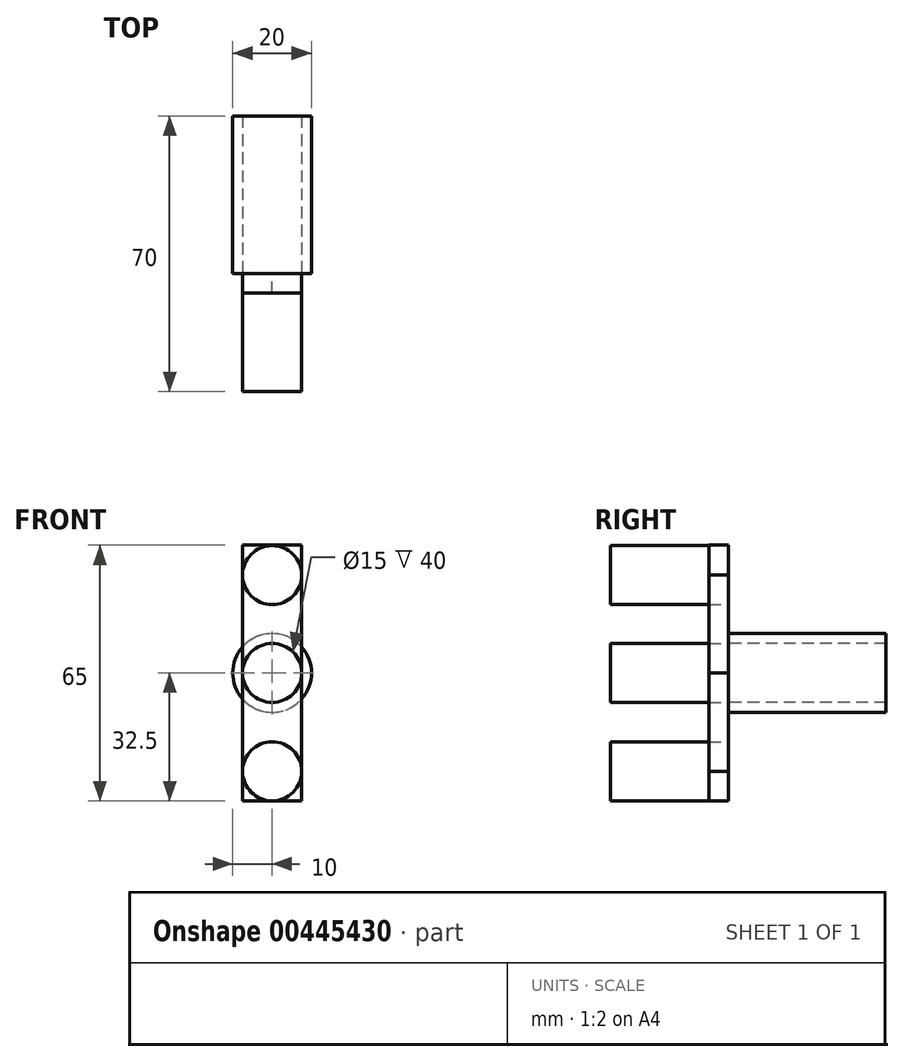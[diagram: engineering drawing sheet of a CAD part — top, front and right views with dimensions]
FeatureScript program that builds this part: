
annotation { "Feature Type Name" : "Feature", "Feature Type Description" : "" }
export const myFeature = defineFeature(function(context is Context, id is Id, definition is map)
    precondition{}
    {
        {
            var Q0;
            Q0=qCreatedBy(makeId("Front.planeOp"),FACE);
            var sketch = newSketch(context, id + "F0", { "sketchPlane" : qUnion([Q0])});
            skLineSegment(sketch, "E0.bottom", {"start": v(-7.5, 32.5) * mm, "end": v(7.5, 32.5) * mm});
            skLineSegment(sketch, "E0.top", {"start": v(-7.5, -32.5) * mm, "end": v(7.5, -32.5) * mm});
            skLineSegment(sketch, "E0.left", {"start": v(-7.5, 32.5) * mm, "end": v(-7.5, -32.5) * mm});
            skLineSegment(sketch, "E0.right", {"start": v(7.5, 32.5) * mm, "end": v(7.5, -32.5) * mm});
            skPoint(sketch, "E0.middle", {"position": v(0, 0) * mm});
            skCircle(sketch, "E1", {"center": v(0, 0) * mm, "radius": 7.5 * mm});
            skLineSegment(sketch, "E2", {"start": v(0, 7.5) * mm, "end": v(0, 17.5) * mm});
            skLineSegment(sketch, "E3", {"start": v(0, -7.5) * mm, "end": v(0, -17.5) * mm});
            skCircle(sketch, "E4", {"center": v(0, -25) * mm, "radius": 7.5 * mm});
            skCircle(sketch, "E5", {"center": v(0, 24.86) * mm, "radius": 7.5 * mm});
            skSolve(sketch);
        }
        {
            var Q0;
            {var subQ0=sQuery(id+"F0.wireOp",EDGE,"E1");var subQ1=makeQuery(id+"F0.imprint","INTERSECT",VERTEX,{"derivedFrom":[subQ0,sQuery(id+"F0.wireOp",EDGE,"E2")]});Q0=makeQuery(id+"F0.imprint","IMPRINT",FACE,{"disambiguationData":[TD([[makeQuery(id+"F0.imprint","IMPRINT",EDGE,{"disambiguationData":[TD([[subQ1,1.0]])],"derivedFrom":subQ0}),1.0]])]});}
            var Q1;
            {var subQ0=sQuery(id+"F0.wireOp",EDGE,"E5");var subQ1=makeQuery(id+"F0.imprint","INTERSECT",VERTEX,{"derivedFrom":[sQuery(id+"F0.wireOp",EDGE,"E0.left"),subQ0]});Q1=makeQuery(id+"F0.imprint","IMPRINT",FACE,{"disambiguationData":[TD([[makeQuery(id+"F0.imprint","IMPRINT",EDGE,{"disambiguationData":[TD([[subQ1,1.0]])],"derivedFrom":subQ0}),1.0]])]});}
            var Q2;
            {var subQ0=sQuery(id+"F0.wireOp",EDGE,"E4");var subQ1=makeQuery(id+"F0.imprint","INTERSECT",VERTEX,{"derivedFrom":[sQuery(id+"F0.wireOp",EDGE,"E3"),subQ0]});Q2=makeQuery(id+"F0.imprint","IMPRINT",FACE,{"disambiguationData":[TD([[makeQuery(id+"F0.imprint","IMPRINT",EDGE,{"disambiguationData":[TD([[subQ1,1.0]])],"derivedFrom":subQ0}),1.0]])]});}
            extrude(context, id + "F1", {"entities" : qUnion([Q0, Q1, Q2]), "depth" : 30 * mm});
        }
        {
            var Q0;
            {var subQ0=sQuery(id+"F0.wireOp",EDGE,"E5");var subQ1=sQuery(id+"F0.wireOp",EDGE,"E0.right");var subQ2=makeQuery(id+"F0.imprint","INTERSECT",VERTEX,{"derivedFrom":[subQ1,subQ0]});Q0=makeQuery(id+"F0.imprint","IMPRINT",FACE,{"disambiguationData":[TD([[makeQuery(id+"F0.imprint","IMPRINT",EDGE,{"disambiguationData":[TD([[subQ2,-1.0]])],"derivedFrom":subQ1}),-1.0]])]});}
            var Q1;
            {var subQ0=sQuery(id+"F0.wireOp",EDGE,"E5");var subQ1=sQuery(id+"F0.wireOp",EDGE,"E0.left");var subQ2=makeQuery(id+"F0.imprint","INTERSECT",VERTEX,{"derivedFrom":[subQ1,subQ0]});Q1=makeQuery(id+"F0.imprint","IMPRINT",FACE,{"disambiguationData":[TD([[makeQuery(id+"F0.imprint","IMPRINT",EDGE,{"disambiguationData":[TD([[subQ2,-1.0]])],"derivedFrom":subQ1}),1.0]])]});}
            var Q2;
            {var subQ0=sQuery(id+"F0.wireOp",EDGE,"E0.bottom");Q2=makeQuery(id+"F0.imprint","IMPRINT",FACE,{"disambiguationData":[TD([[makeQuery(id+"F0.imprint","IMPRINT",EDGE,{"derivedFrom":subQ0}),-1.0]])]});}
            var Q3;
            {var subQ5=sQuery(id+"F0.wireOp",EDGE,"E3");Q3=makeQuery(id+"F0.imprint","IMPRINT",FACE,{"disambiguationData":[TD([[makeQuery(id+"F0.imprint","IMPRINT",EDGE,{"derivedFrom":subQ5}),1.0]])]});}
            var Q4;
            {var subQ5=sQuery(id+"F0.wireOp",EDGE,"E3");Q4=makeQuery(id+"F0.imprint","IMPRINT",FACE,{"disambiguationData":[TD([[makeQuery(id+"F0.imprint","IMPRINT",EDGE,{"derivedFrom":subQ5}),-1.0]])]});}
            var Q5;
            {var subQ0=sQuery(id+"F0.wireOp",EDGE,"E0.left");var subQ1=sQuery(id+"F0.wireOp",EDGE,"E0.top");var subQ2=makeQuery(id+"F0.imprint","INTERSECT",VERTEX,{"derivedFrom":[subQ1,subQ0]});Q5=makeQuery(id+"F0.imprint","IMPRINT",FACE,{"disambiguationData":[TD([[makeQuery(id+"F0.imprint","IMPRINT",EDGE,{"disambiguationData":[TD([[subQ2,-1.0]])],"derivedFrom":subQ1}),1.0]])]});}
            var Q6;
            {var subQ0=sQuery(id+"F0.wireOp",EDGE,"E0.right");var subQ1=sQuery(id+"F0.wireOp",EDGE,"E0.top");var subQ2=makeQuery(id+"F0.imprint","INTERSECT",VERTEX,{"derivedFrom":[subQ1,subQ0]});Q6=makeQuery(id+"F0.imprint","IMPRINT",FACE,{"disambiguationData":[TD([[makeQuery(id+"F0.imprint","IMPRINT",EDGE,{"disambiguationData":[TD([[subQ2,1.0]])],"derivedFrom":subQ1}),1.0]])]});}
            extrude(context, id + "F2", {"entities" : qUnion([Q0, Q1, Q2, Q3, Q4, Q5, Q6]), "depth" : 5 * mm});
        }
        {
            var Q0;
            {var subQ0=sQuery(id+"F0.wireOp",EDGE,"E1");var subQ1=makeQuery(id+"F0.imprint","INTERSECT",VERTEX,{"derivedFrom":[subQ0,sQuery(id+"F0.wireOp",EDGE,"E2")]});Q0=makeQuery(id+"F0.imprint","IMPRINT",FACE,{"disambiguationData":[TD([[makeQuery(id+"F0.imprint","IMPRINT",EDGE,{"disambiguationData":[TD([[subQ1,1.0]])],"derivedFrom":subQ0}),1.0]])]});}
            var sketch = newSketch(context, id + "F3", { "sketchPlane" : qUnion([Q0])});
            skCircle(sketch, "E6", {"center": v(0, 0) * mm, "radius": 10 * mm});
            skSolve(sketch);
        }
        {
            var Q0;
            Q0=makeQuery(id+"F3.imprint","IMPRINT",FACE,{"disambiguationData":[TD([[makeQuery(id+"F3.imprint","IMPRINT",EDGE,{"derivedFrom":sQuery(id+"F3.wireOp",EDGE,"E6")}),1.0]])]});
            extrude(context, id + "F4", {"entities" : qUnion([Q0]), "oppositeDirection" : true, "depth" : 40 * mm});
        }
    });
